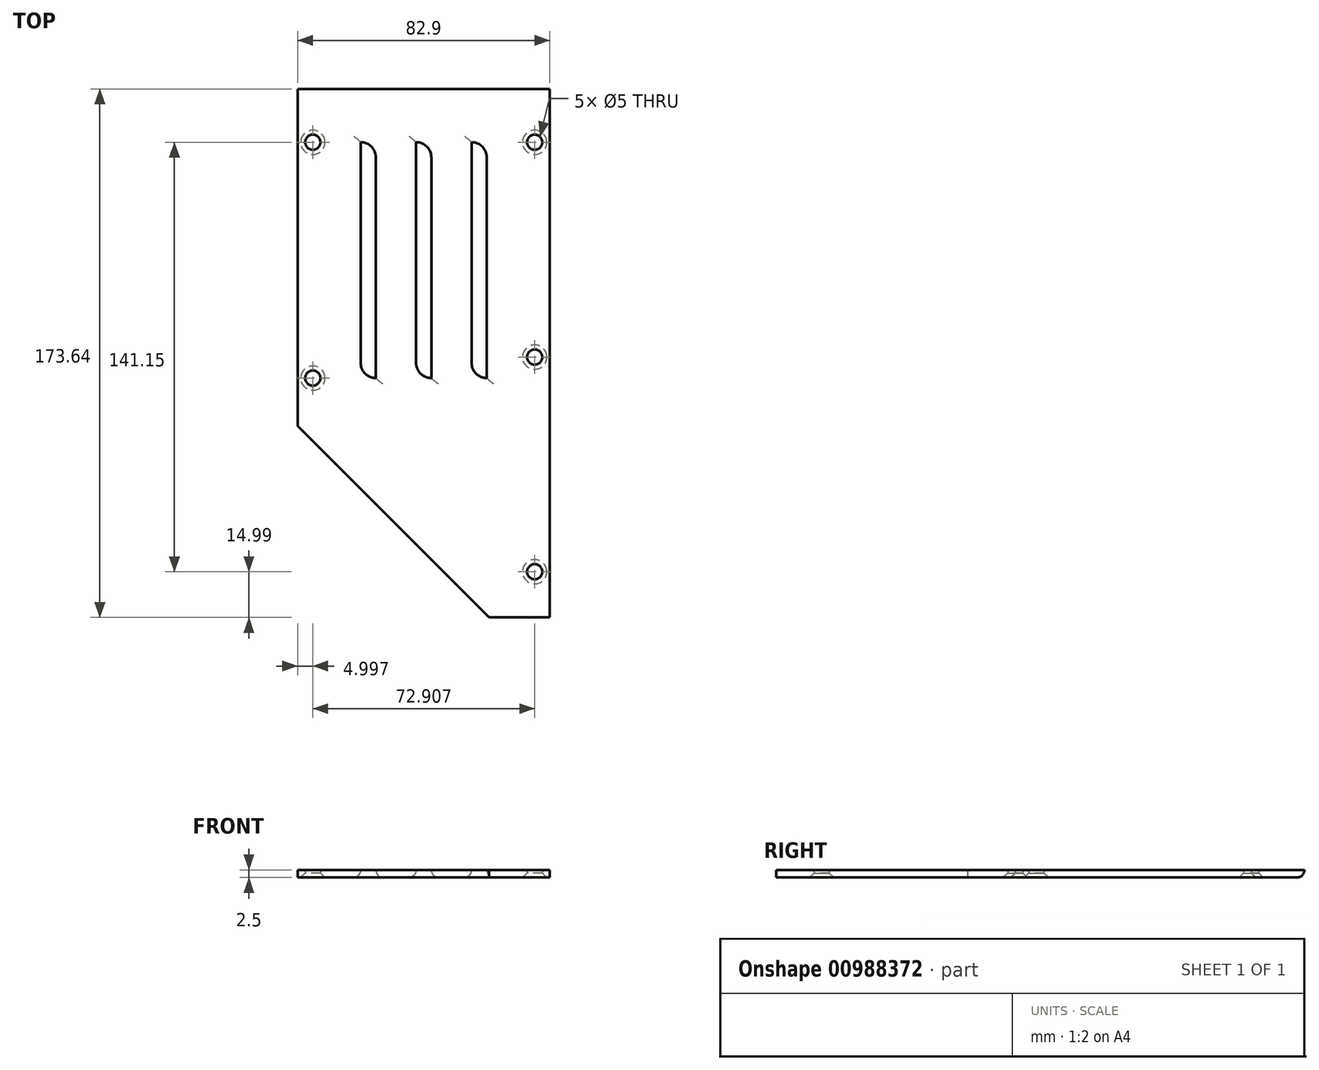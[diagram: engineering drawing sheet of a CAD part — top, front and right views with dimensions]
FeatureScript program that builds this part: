
annotation { "Feature Type Name" : "Feature", "Feature Type Description" : "" }
export const myFeature = defineFeature(function(context is Context, id is Id, definition is map)
    precondition{}
    {
        {
            var Q0;
            Q0=qCreatedBy(makeId("Top.planeOp"),FACE);
            var sketch = newSketch(context, id + "F0", { "sketchPlane" : qUnion([Q0])});
            skPoint(sketch, "E0", {"position": v(-41.45, 86.82) * mm});
            skLineSegment(sketch, "E1.bottom", {"start": v(-41.45, 86.82) * mm, "end": v(41.45, 86.82) * mm});
            skLineSegment(sketch, "E1.top", {"start": v(21.45, -86.82) * mm, "end": v(41.45, -86.82) * mm});
            skLineSegment(sketch, "E1.left", {"start": v(-41.45, 86.82) * mm, "end": v(-41.45, -23.91) * mm});
            skLineSegment(sketch, "E1.right", {"start": v(41.45, 86.82) * mm, "end": v(41.45, -86.82) * mm});
            skLineSegment(sketch, "E2", {"start": v(-41.45, -23.91) * mm, "end": v(21.45, -86.82) * mm});
            skCircle(sketch, "E3", {"center": v(-36.45, 69.32) * mm, "radius": 2.5 * mm});
            skCircle(sketch, "E4", {"center": v(-36.45, -8.18) * mm, "radius": 2.5 * mm});
            skCircle(sketch, "E5", {"center": v(36.45, -71.83) * mm, "radius": 2.5 * mm});
            skCircle(sketch, "E6", {"center": v(36.45, -1.28) * mm, "radius": 2.5 * mm});
            skCircle(sketch, "E7", {"center": v(36.45, 69.32) * mm, "radius": 2.5 * mm});
            skLineSegment(sketch, "E8", {"start": v(-20.73, 69.33) * mm, "end": v(-20.73, -3.2) * mm});
            skLineSegment(sketch, "E9", {"start": v(-15.73, 64.32) * mm, "end": v(-15.73, -8.18) * mm});
            skArc(sketch, "E10", {"start": v(-15.73, 64.32) * mm, "mid": v(-17.2, 67.86) * mm, "end": v(-20.73, 69.33) * mm});
            skArc(sketch, "E11", {"start": v(-20.73, -3.2) * mm, "mid": v(-19.26, -6.73) * mm, "end": v(-15.73, -8.18) * mm});
            skLineSegment(sketch, "E12.1.0.0", {"start": v(-2.5, 69.33) * mm, "end": v(-2.5, -3.2) * mm});
            skArc(sketch, "E12.1.0.1", {"start": v(2.5, 64.32) * mm, "mid": v(1.03, 67.86) * mm, "end": v(-2.5, 69.33) * mm});
            skArc(sketch, "E12.1.0.2", {"start": v(-2.5, -3.2) * mm, "mid": v(-1.04, -6.73) * mm, "end": v(2.5, -8.18) * mm});
            skLineSegment(sketch, "E12.1.0.3", {"start": v(2.5, 64.32) * mm, "end": v(2.5, -8.18) * mm});
            skLineSegment(sketch, "E12.2.0.0", {"start": v(15.72, 69.33) * mm, "end": v(15.72, -3.2) * mm});
            skArc(sketch, "E12.2.0.1", {"start": v(20.72, 64.32) * mm, "mid": v(19.26, 67.86) * mm, "end": v(15.72, 69.33) * mm});
            skArc(sketch, "E12.2.0.2", {"start": v(15.72, -3.2) * mm, "mid": v(17.19, -6.73) * mm, "end": v(20.72, -8.18) * mm});
            skLineSegment(sketch, "E12.2.0.3", {"start": v(20.72, 64.32) * mm, "end": v(20.72, -8.18) * mm});
            skLineSegment(sketch, "E12.direction1", {"start": v(-15.73, -8.18) * mm, "end": v(2.5, -8.18) * mm, "construction": true});
            skSolve(sketch);
        }
        {
            var Q0;
            Q0 = qSketchRegion(id + "F0", true);
            extrude(context, id + "F1", {"entities" : qUnion([Q0]), "endBound" : BoundingType.SYMMETRIC, "depth" : 2.5 * mm, "offsetDistance" : 25 * mm});
        }
        {
            var Q0;
            Q0=makeQuery(id+"F1.opExtrude","CAP_EDGE",EDGE,{"disambiguationData":[OSD([sQuery(id+"F0.wireOp",EDGE,"E1.bottom")])],"isStart":true});
            var Q1;
            Q1=makeQuery(id+"F1.opExtrude","CAP_EDGE",EDGE,{"disambiguationData":[OSD([sQuery(id+"F0.wireOp",EDGE,"E12.1.0.0")])],"isStart":true});
            var Q2;
            Q2=makeQuery(id+"F1.opExtrude","CAP_EDGE",EDGE,{"disambiguationData":[OSD([sQuery(id+"F0.wireOp",EDGE,"E12.1.0.3")])],"isStart":true});
            var Q3;
            Q3=makeQuery(id+"F1.opExtrude","CAP_EDGE",EDGE,{"disambiguationData":[OSD([sQuery(id+"F0.wireOp",EDGE,"E8")])],"isStart":true});
            var Q4;
            Q4=makeQuery(id+"F1.opExtrude","CAP_EDGE",EDGE,{"disambiguationData":[OSD([sQuery(id+"F0.wireOp",EDGE,"E9")])],"isStart":true});
            var Q5;
            Q5=makeQuery(id+"F1.opExtrude","CAP_EDGE",EDGE,{"disambiguationData":[OSD([sQuery(id+"F0.wireOp",EDGE,"E12.2.0.0")])],"isStart":true});
            var Q6;
            Q6=makeQuery(id+"F1.opExtrude","CAP_EDGE",EDGE,{"disambiguationData":[OSD([sQuery(id+"F0.wireOp",EDGE,"E12.2.0.3")])],"isStart":true});
            fillet(context, id + "F2", {"entities" : qUnion([Q0, Q1, Q2, Q3, Q4, Q5, Q6]), "radius" : 2.5 * mm, "tangentPropagation" : true, "allowEdgeOverflow" : false});
        }
        {
            var Q0;
            Q0=makeQuery(id+"F1.opExtrude","CAP_EDGE",EDGE,{"disambiguationData":[OSD([sQuery(id+"F0.wireOp",EDGE,"E3")])],"isStart":true});
            var Q1;
            Q1=makeQuery(id+"F1.opExtrude","CAP_EDGE",EDGE,{"disambiguationData":[OSD([sQuery(id+"F0.wireOp",EDGE,"E7")])],"isStart":true});
            var Q2;
            Q2=makeQuery(id+"F1.opExtrude","CAP_EDGE",EDGE,{"disambiguationData":[OSD([sQuery(id+"F0.wireOp",EDGE,"E6")])],"isStart":true});
            var Q3;
            Q3=makeQuery(id+"F1.opExtrude","CAP_EDGE",EDGE,{"disambiguationData":[OSD([sQuery(id+"F0.wireOp",EDGE,"E4")])],"isStart":true});
            var Q4;
            Q4=makeQuery(id+"F1.opExtrude","CAP_EDGE",EDGE,{"disambiguationData":[OSD([sQuery(id+"F0.wireOp",EDGE,"E5")])],"isStart":true});
            chamfer(context, id + "F3", {"entities" : qUnion([Q0, Q1, Q2, Q3, Q4]), "width" : 1.5 * mm, "tangentPropagation" : true});
        }
    });
